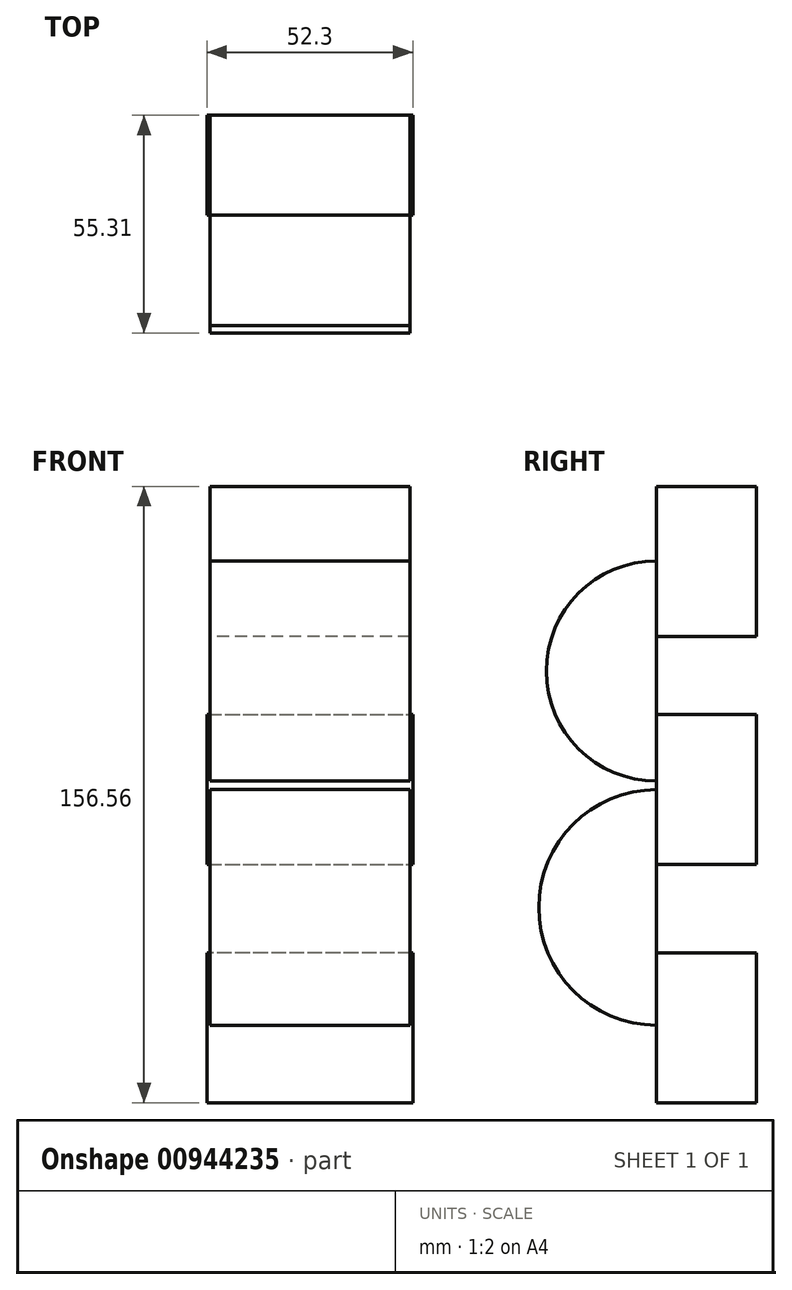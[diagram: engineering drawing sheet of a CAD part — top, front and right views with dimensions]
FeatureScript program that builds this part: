
annotation { "Feature Type Name" : "Feature", "Feature Type Description" : "" }
export const myFeature = defineFeature(function(context is Context, id is Id, definition is map)
    precondition{}
    {
        {
            var Q0;
            Q0=qCreatedBy(makeId("Front.planeOp"),FACE);
            var sketch = newSketch(context, id + "F0", { "sketchPlane" : qUnion([Q0])});
            skLineSegment(sketch, "E0.bottom", {"start": v(-26.15, 19.05) * mm, "end": v(26.15, 19.05) * mm});
            skLineSegment(sketch, "E0.top", {"start": v(-26.15, -19.05) * mm, "end": v(26.15, -19.05) * mm});
            skLineSegment(sketch, "E0.left", {"start": v(-26.15, 19.05) * mm, "end": v(-26.15, -19.05) * mm});
            skLineSegment(sketch, "E0.right", {"start": v(26.15, 19.05) * mm, "end": v(26.15, -19.05) * mm});
            skPoint(sketch, "E0.middle", {"position": v(0, 0) * mm});
            skLineSegment(sketch, "E1.bottom", {"start": v(25.4, 38.94) * mm, "end": v(-25.4, 38.94) * mm});
            skLineSegment(sketch, "E1.top", {"start": v(25.4, 77.04) * mm, "end": v(-25.4, 77.04) * mm});
            skLineSegment(sketch, "E1.left", {"start": v(25.4, 38.94) * mm, "end": v(25.4, 77.04) * mm});
            skLineSegment(sketch, "E1.right", {"start": v(-25.4, 38.94) * mm, "end": v(-25.4, 77.04) * mm});
            skPoint(sketch, "E1.middle", {"position": v(0, 57.99) * mm});
            skLineSegment(sketch, "E2.bottom", {"start": v(26.15, -79.52) * mm, "end": v(-26.15, -79.52) * mm});
            skLineSegment(sketch, "E2.top", {"start": v(26.15, -41.42) * mm, "end": v(-26.15, -41.42) * mm});
            skLineSegment(sketch, "E2.left", {"start": v(26.15, -79.52) * mm, "end": v(26.15, -41.42) * mm});
            skLineSegment(sketch, "E2.right", {"start": v(-26.15, -79.52) * mm, "end": v(-26.15, -41.42) * mm});
            skPoint(sketch, "E2.middle", {"position": v(0, -60.47) * mm});
            skSolve(sketch);
        }
        {
            var Q0;
            Q0=qCreatedBy(makeId("Right.planeOp"),FACE);
            var sketch = newSketch(context, id + "F1", { "sketchPlane" : qUnion([Q0])});
            skArc(sketch, "E3", {"start": v(0, 58.12) * mm, "mid": v(-27.97, 30.15) * mm, "end": v(0, 2.17) * mm});
            skArc(sketch, "E4", {"start": v(0, 0) * mm, "mid": v(-29.91, -29.91) * mm, "end": v(0, -59.83) * mm});
            skLineSegment(sketch, "E5", {"start": v(0, 58.12) * mm, "end": v(0, 2.17) * mm});
            skLineSegment(sketch, "E6", {"start": v(0, 0) * mm, "end": v(0, -59.83) * mm});
            skSolve(sketch);
        }
        {
            var Q0;
            Q0=makeQuery(id+"F0.imprint","IMPRINT",FACE,{"disambiguationData":[TD([[makeQuery(id+"F0.imprint","IMPRINT",EDGE,{"derivedFrom":sQuery(id+"F0.wireOp",EDGE,"E1.bottom")}),-1.0]])]});
            var Q1;
            Q1=makeQuery(id+"F0.imprint","IMPRINT",FACE,{"disambiguationData":[TD([[makeQuery(id+"F0.imprint","IMPRINT",EDGE,{"derivedFrom":sQuery(id+"F0.wireOp",EDGE,"E0.bottom")}),-1.0]])]});
            var Q2;
            Q2=makeQuery(id+"F0.imprint","IMPRINT",FACE,{"disambiguationData":[TD([[makeQuery(id+"F0.imprint","IMPRINT",EDGE,{"derivedFrom":sQuery(id+"F0.wireOp",EDGE,"E2.bottom")}),-1.0]])]});
            extrude(context, id + "F2", {"entities" : qUnion([Q0, Q1, Q2]), "oppositeDirection" : true, "depth" : 25.4 * mm, "offsetDistance" : 25.4 * mm});
        }
        {
            var Q0;
            Q0=makeQuery(id+"F1.imprint","IMPRINT",FACE,{"disambiguationData":[TD([[makeQuery(id+"F1.imprint","IMPRINT",EDGE,{"derivedFrom":sQuery(id+"F1.wireOp",EDGE,"E4")}),1.0]])]});
            var Q1;
            Q1=makeQuery(id+"F1.imprint","IMPRINT",FACE,{"disambiguationData":[TD([[makeQuery(id+"F1.imprint","IMPRINT",EDGE,{"derivedFrom":sQuery(id+"F1.wireOp",EDGE,"E3")}),1.0]])]});
            extrude(context, id + "F3", {"entities" : qUnion([Q0, Q1]), "endBound" : BoundingType.SYMMETRIC, "depth" : 50.8 * mm, "offsetDistance" : 25.4 * mm});
        }
    });
